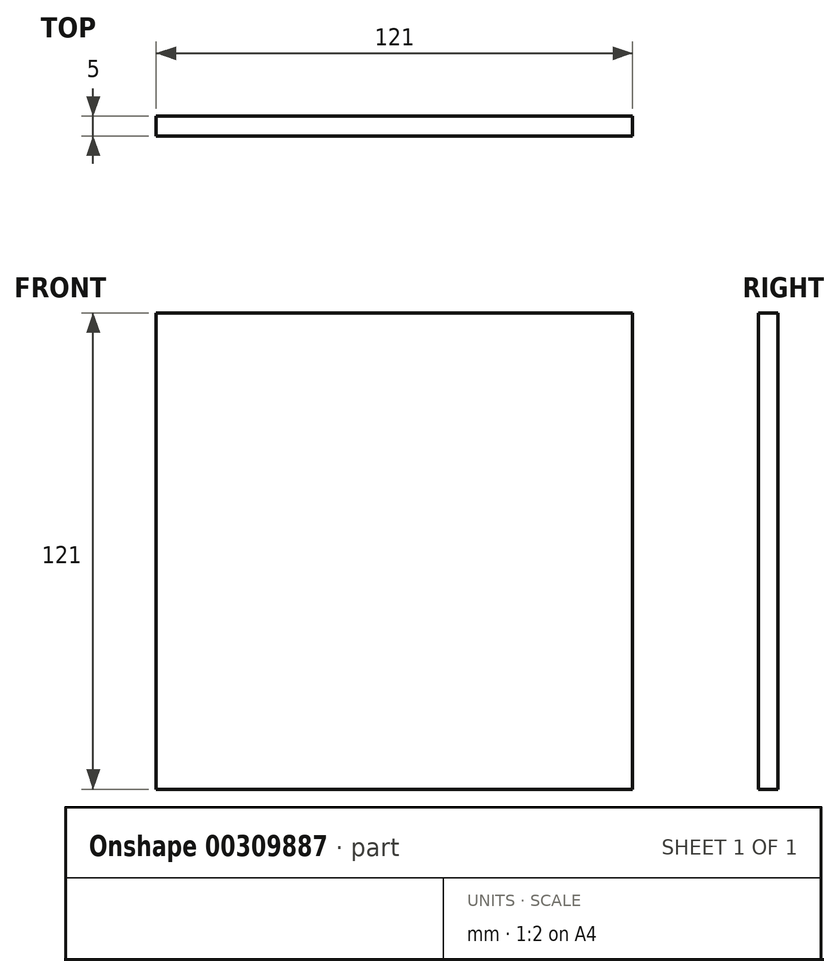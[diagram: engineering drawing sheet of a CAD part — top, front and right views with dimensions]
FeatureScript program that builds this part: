
annotation { "Feature Type Name" : "Feature", "Feature Type Description" : "" }
export const myFeature = defineFeature(function(context is Context, id is Id, definition is map)
    precondition{}
    {
        {
            var Q0;
            Q0=qCreatedBy(makeId("Front.planeOp"),FACE);
            var sketch = newSketch(context, id + "F0", { "sketchPlane" : qUnion([Q0])});
            skLineSegment(sketch, "E0.bottom", {"start": v(-60.5, 60.5) * mm, "end": v(60.5, 60.5) * mm});
            skLineSegment(sketch, "E0.top", {"start": v(-60.5, -60.5) * mm, "end": v(60.5, -60.5) * mm});
            skLineSegment(sketch, "E0.left", {"start": v(-60.5, 60.5) * mm, "end": v(-60.5, -60.5) * mm});
            skLineSegment(sketch, "E0.right", {"start": v(60.5, 60.5) * mm, "end": v(60.5, -60.5) * mm});
            skPoint(sketch, "E0.middle", {"position": v(0, 0) * mm});
            skSolve(sketch);
        }
        {
            var Q0;
            Q0=makeQuery(id+"F0.imprint","IMPRINT",FACE,{"disambiguationData":[TD([[makeQuery(id+"F0.imprint","IMPRINT",EDGE,{"derivedFrom":sQuery(id+"F0.wireOp",EDGE,"E0.bottom")}),-1.0]])]});
            extrude(context, id + "F1", {"entities" : qUnion([Q0]), "depth" : 5 * mm});
        }
    });
